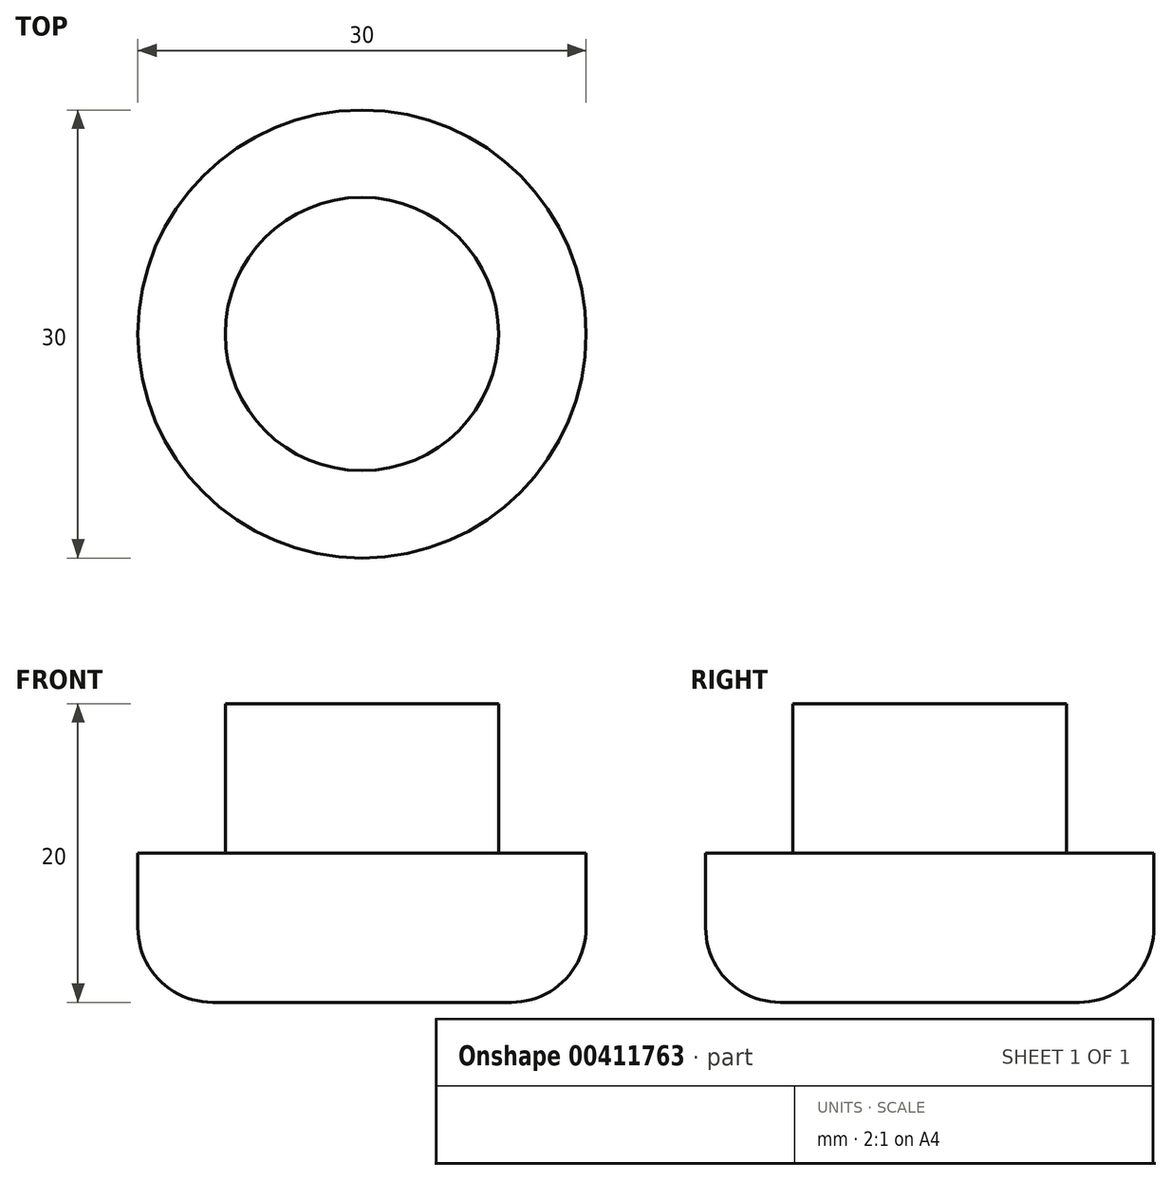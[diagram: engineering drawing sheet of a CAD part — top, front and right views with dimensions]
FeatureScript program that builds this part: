
annotation { "Feature Type Name" : "Feature", "Feature Type Description" : "" }
export const myFeature = defineFeature(function(context is Context, id is Id, definition is map)
    precondition{}
    {
        {
            var Q0;
            Q0=qCreatedBy(makeId("Top.planeOp"),FACE);
            var sketch = newSketch(context, id + "F0", { "sketchPlane" : qUnion([Q0])});
            skCircle(sketch, "E0", {"center": v(0, 0) * mm, "radius": 15 * mm});
            skSolve(sketch);
        }
        {
            var Q0;
            Q0 = qSketchRegion(id + "F0", true);
            extrude(context, id + "F1", {"entities" : qUnion([Q0]), "depth" : 10 * mm});
        }
        {
            var Q0;
            Q0=makeQuery(id+"F1.opExtrude","CAP_FACE",FACE,{"disambiguationData":[OSD([sQuery(id+"F0.wireOp",EDGE,"E0")])],"isStart":false});
            cPlane(context, id + "F2", {"entities" : qUnion([Q0]), "cplaneType" : CPlaneType.OFFSET, "offset" : 0 * mm, "width" : 150 * mm, "height" : 150 * mm});
        }
        {
            var Q0;
            Q0=qCreatedBy(id+"F2.planeOp",FACE);
            var sketch = newSketch(context, id + "F3", { "sketchPlane" : qUnion([Q0])});
            skCircle(sketch, "E1", {"center": v(0, 0) * mm, "radius": 9.15 * mm});
            skSolve(sketch);
        }
        {
            var Q0;
            Q0 = qSketchRegion(id + "F3", true);
            extrude(context, id + "F4", {"entities" : qUnion([Q0]), "operationType" : NewBodyOperationType.ADD, "depth" : 10 * mm});
        }
        {
            var Q0;
            Q0=makeQuery(id+"F1.opExtrude","CAP_EDGE",EDGE,{"disambiguationData":[OSD([sQuery(id+"F0.wireOp",EDGE,"E0")])],"isStart":true});
            fillet(context, id + "F5", {"entities" : qUnion([Q0]), "radius" : 5 * mm, "tangentPropagation" : true, "allowEdgeOverflow" : false});
        }
    });
